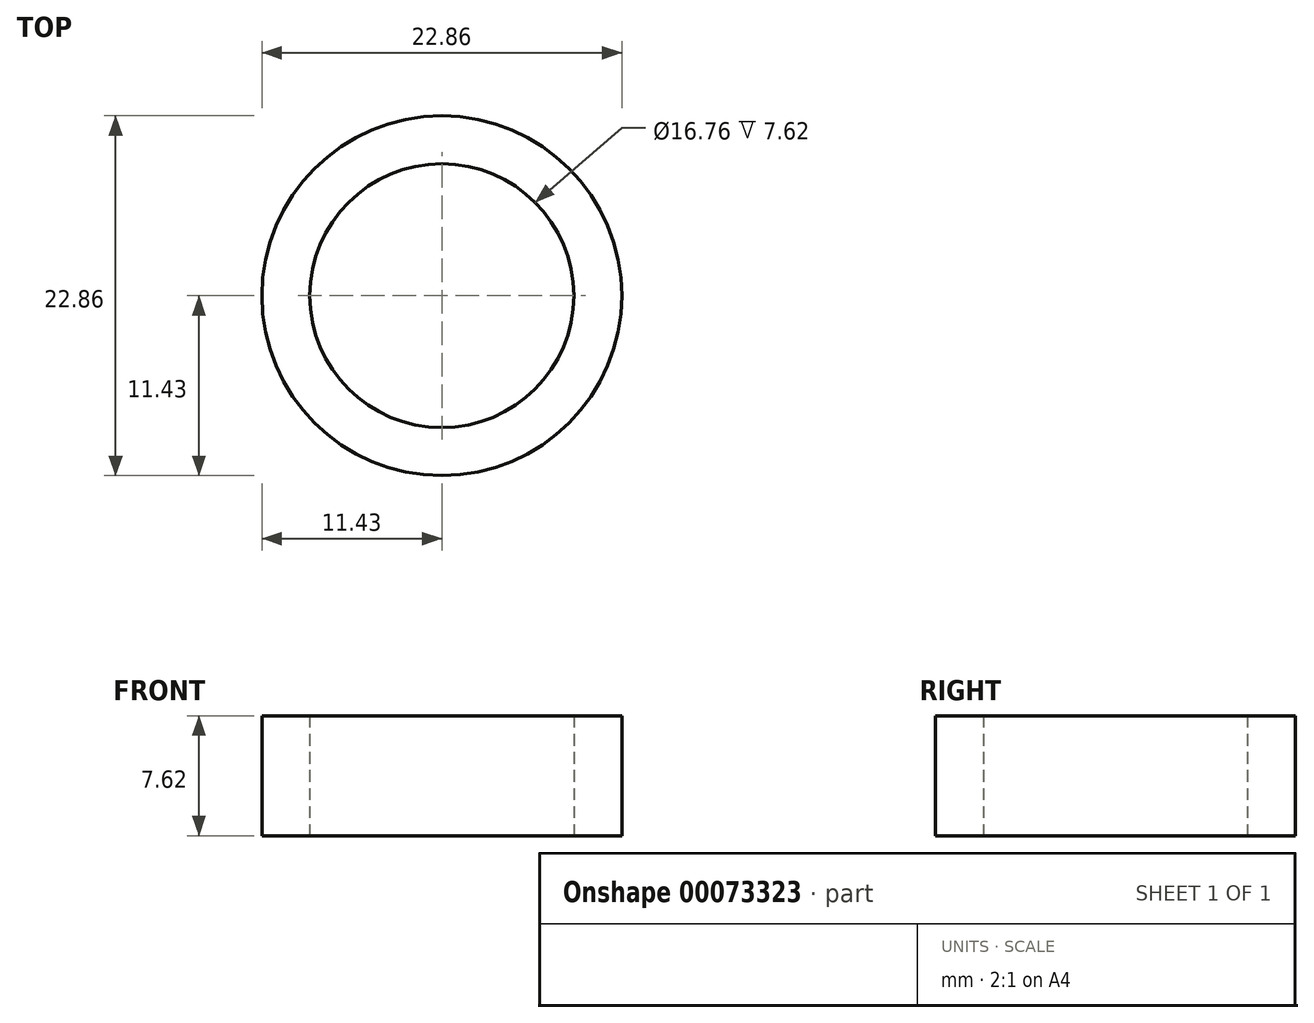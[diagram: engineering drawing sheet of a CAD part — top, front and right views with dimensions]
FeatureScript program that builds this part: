
annotation { "Feature Type Name" : "Feature", "Feature Type Description" : "" }
export const myFeature = defineFeature(function(context is Context, id is Id, definition is map)
    precondition{}
    {
        {
            var Q0;
            Q0=qCreatedBy(makeId("Top.planeOp"),FACE);
            var sketch = newSketch(context, id + "F0", { "sketchPlane" : qUnion([Q0])});
            skCircle(sketch, "E0", {"center": v(0, 0) * mm, "radius": 11.43 * mm});
            skCircle(sketch, "E1", {"center": v(0, 0) * mm, "radius": 8.38 * mm});
            skSolve(sketch);
        }
        {
            var Q0;
            Q0 = qSketchRegion(id + "F0", true);
            extrude(context, id + "F1", {"entities" : qUnion([Q0]), "depth" : 7.62 * mm});
        }
    });
